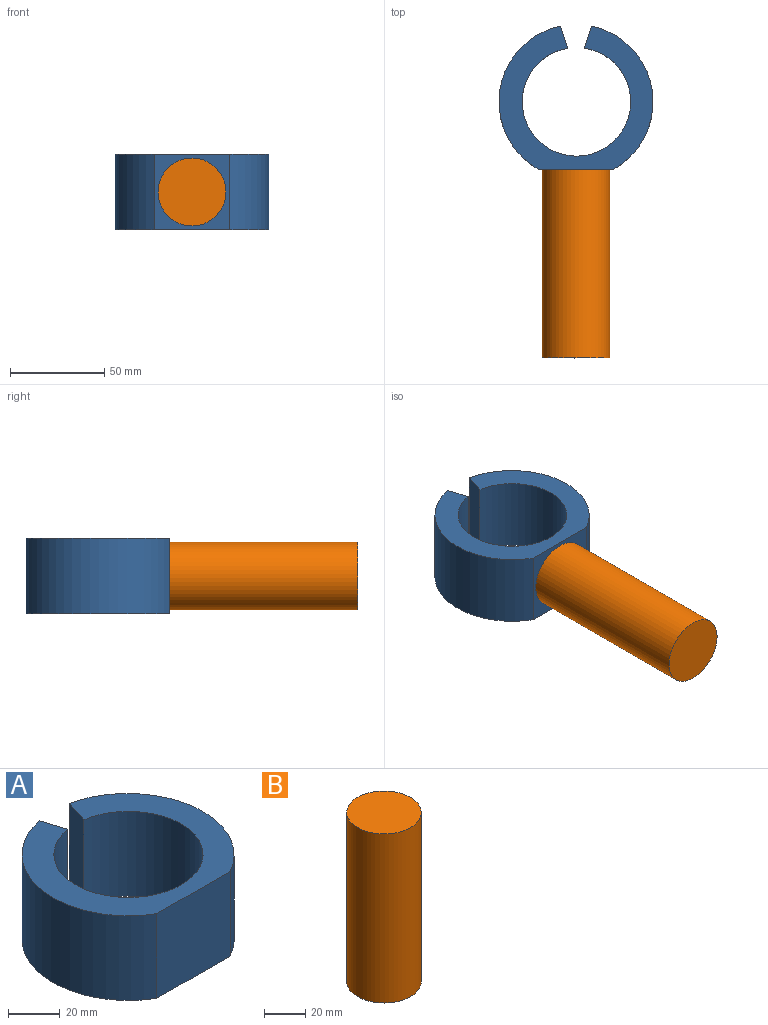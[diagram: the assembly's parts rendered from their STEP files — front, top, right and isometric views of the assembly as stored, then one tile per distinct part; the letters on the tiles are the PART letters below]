
ASSEMBLY  parts=2 mates=1
PART A: 8 faces, bbox 81.7x76x40 mm
  f0: cylinder r=28.79mm len=57.57mm, axis (0,0,-1), area 6882.1mm2, adj f1,f5,f6,f7
  f1: plane 40x11.82mm, normal (0.95,0.3,0), area 496mm2, adj f0,f2,f6,f7
  f2: cylinder r=41.1mm len=75.99mm, axis (0,0,-1), area 3979.6mm2, adj f1,f3,f6,f7
  f3: plane 40x40mm, normal (0,-1,0), area 1600mm2, adj f2,f4,f6,f7
  f4: cylinder r=41.1mm len=75.99mm, axis (0,0,-1), area 3979.6mm2, adj f3,f5,f6,f7
  f5: plane 40x11.75mm, normal (-0.95,0.3,0), area 493mm2, adj f0,f4,f6,f7
  f6: plane 81.7x75.99mm, normal (0,0,1), area 2363.4mm2, adj f0,f1,f2,f3,f4,f5
  f7: plane 81.7x75.99mm, normal (0,0,-1), area 2363.4mm2, adj f0,f1,f2,f3,f4,f5
PART B: 3 faces, bbox 36x36x100 mm
  f0: cylinder r=18mm len=100mm, axis (0,0,-1), area 11309.7mm2, adj f1,f2
  f1: plane 36x36mm, normal (0,0,1), area 1017.9mm2, adj f0
  f2: plane 36x36mm, normal (0,0,-1), area 1017.9mm2, adj f0
PLACE A t=(48.21,56.35,42.27)mm
PLACE B rot(axis=(-1,0,0),90deg) t=(48.21,-68.65,62.27)mm
MATE cylindrical B.f0 <-> A.f3  axis (0,1,0) through (48.21,31.35,62.27)mm
